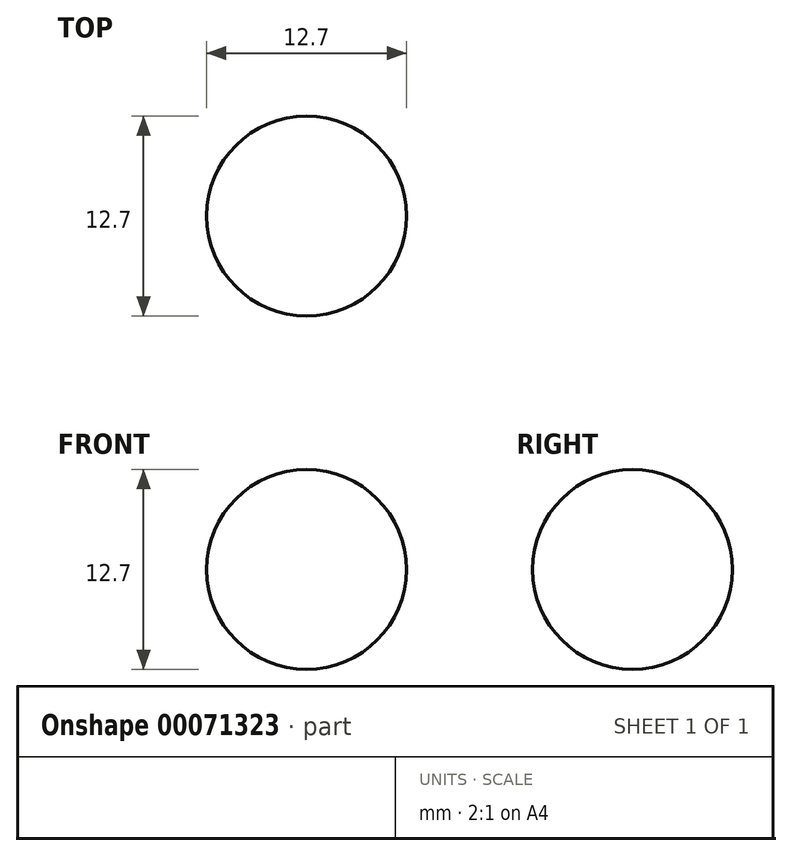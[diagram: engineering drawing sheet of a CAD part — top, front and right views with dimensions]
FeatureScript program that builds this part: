
annotation { "Feature Type Name" : "Feature", "Feature Type Description" : "" }
export const myFeature = defineFeature(function(context is Context, id is Id, definition is map)
    precondition{}
    {
        {
            var Q0;
            Q0=qCreatedBy(makeId("Front.planeOp"),FACE);
            var sketch = newSketch(context, id + "F0", { "sketchPlane" : qUnion([Q0])});
            skLineSegment(sketch, "E0", {"start": v(0, 0) * mm, "end": v(0, -6.35) * mm});
            skArc(sketch, "E1", {"start": v(0, -6.35) * mm, "mid": v(-6.35, 0) * mm, "end": v(0, 6.35) * mm});
            skSolve(sketch);
        }
        {
            var Q0;
            Q0=makeQuery(id+"F0.imprint","IMPRINT",FACE,{"disambiguationData":[TD([[makeQuery(id+"F0.imprint","IMPRINT",EDGE,{"derivedFrom":sQuery(id+"F0.wireOp",EDGE,"f575378c-fca0-4022-b559-c717ae973c29")}),1.0]])]});
            var Q1;
            Q1=sQuery(id+"F0.wireOp",EDGE,"E1");
            var Q2;
            Q2=sQuery(id+"F0.wireOp",EDGE,"E0");
            revolve(context, id + "F1", {"bodyType" : ToolBodyType.SURFACE, "entities" : qUnion([Q0]), "surfaceEntities" : qUnion([Q1]), "axis" : qUnion([Q2]), "revolveType" : RevolveType.FULL});
        }
    });
